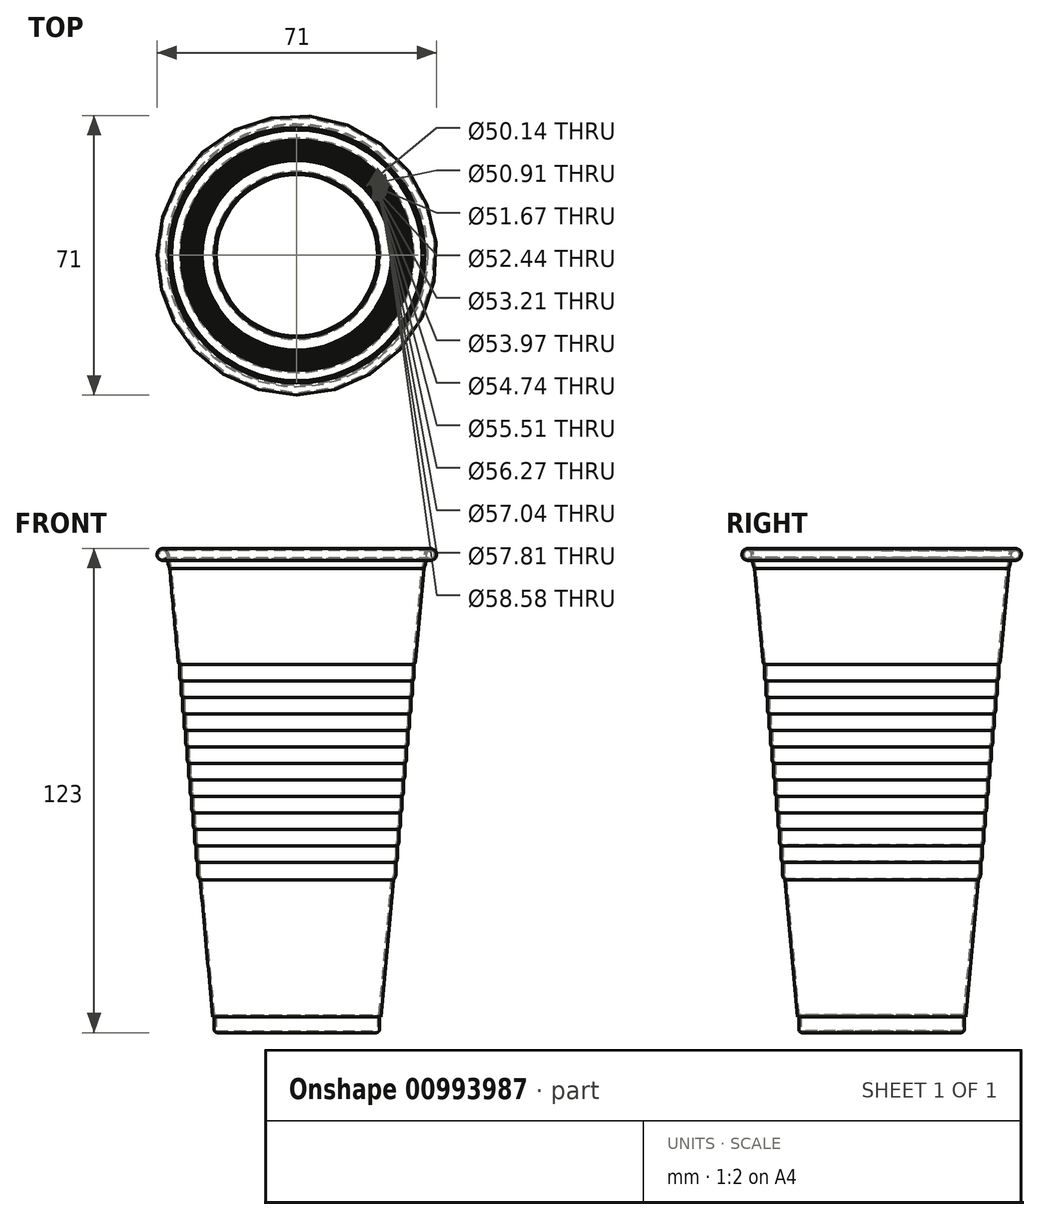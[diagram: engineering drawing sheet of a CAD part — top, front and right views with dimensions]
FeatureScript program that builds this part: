
annotation { "Feature Type Name" : "Feature", "Feature Type Description" : "" }
export const myFeature = defineFeature(function(context is Context, id is Id, definition is map)
    precondition{}
    {
        {
            var Q0;
            Q0=qCreatedBy(makeId("Front.planeOp"),FACE);
            var sketch = newSketch(context, id + "F0", { "sketchPlane" : qUnion([Q0])});
            skLineSegment(sketch, "E0", {"start": v(0, 0) * mm, "end": v(-21, 0) * mm});
            skLineSegment(sketch, "E1", {"start": v(-35.5, 123) * mm, "end": v(-32.27, 123) * mm});
            skLineSegment(sketch, "E2", {"start": v(-35.5, 123) * mm, "end": v(-35.5, 120) * mm});
            skLineSegment(sketch, "E3", {"start": v(-35.5, 120) * mm, "end": v(-32.5, 120) * mm});
            skLineSegment(sketch, "E4", {"start": v(-32.5, 120) * mm, "end": v(-25.18, 40.1) * mm});
            skPoint(sketch, "E5.centerSnap0", {"position": v(-35.5, 121.5) * mm});
            skLineSegment(sketch, "E6", {"start": v(-32.27, 123) * mm, "end": v(-29.67, 94.55) * mm});
            skLineSegment(sketch, "E7", {"start": v(0, 0) * mm, "end": v(0, 0.5) * mm});
            skLineSegment(sketch, "E8", {"start": v(0, 0.5) * mm, "end": v(-20.5, 0.5) * mm});
            skLineSegment(sketch, "E9", {"start": v(-21, 0) * mm, "end": v(-21, 4) * mm});
            skLineSegment(sketch, "E10", {"start": v(-21, 4) * mm, "end": v(-21.37, 4) * mm});
            skLineSegment(sketch, "E11", {"start": v(-20.91, 4.5) * mm, "end": v(-20.5, 4.5) * mm});
            skLineSegment(sketch, "E12", {"start": v(-20.5, 4.5) * mm, "end": v(-20.5, 0.5) * mm});
            skPoint(sketch, "E13.orphan", {"position": v(0, 123) * mm});
            skLineSegment(sketch, "E14", {"start": v(0, 0) * mm, "end": v(0, 123) * mm, "construction": true});
            skCircle(sketch, "E15", {"center": v(-34, 121.5) * mm, "radius": 1.5 * mm});
            skArc(sketch, "E16", {"start": v(-32.5, 121.5) * mm, "mid": v(-32.33, 119.72) * mm, "end": v(-31.81, 118) * mm});
            skCircle(sketch, "E17", {"center": v(-34, 121.5) * mm, "radius": 1 * mm});
            skArc(sketch, "E18", {"start": v(-33, 121.5) * mm, "mid": v(-32.82, 119.66) * mm, "end": v(-32.3, 117.88) * mm});
            skLineSegment(sketch, "E19", {"start": v(-34, 121.5) * mm, "end": v(-32.94, 120.44) * mm});
            skLineSegment(sketch, "E20", {"start": v(-32.5, 121.5) * mm, "end": v(-32.5, 120) * mm});
            skLineSegment(sketch, "E21", {"start": v(-34, 121.5) * mm, "end": v(-33, 121.5) * mm});
            skArc(sketch, "E22", {"start": v(-30.16, 94.5) * mm, "mid": v(-30.04, 93.97) * mm, "end": v(-29.79, 93.5) * mm});
            skPoint(sketch, "E23", {"position": v(-30.16, 94.5) * mm});
            skArc(sketch, "E24", {"start": v(-29.79, 90.5) * mm, "mid": v(-29.69, 89.88) * mm, "end": v(-29.4, 89.32) * mm});
            skLineSegment(sketch, "E25", {"start": v(-29.79, 93.5) * mm, "end": v(-29.79, 90.5) * mm});
            skArc(sketch, "E26", {"start": v(-29.4, 86.32) * mm, "mid": v(-29.3, 85.7) * mm, "end": v(-29.02, 85.13) * mm});
            skLineSegment(sketch, "E27", {"start": v(-29.4, 89.32) * mm, "end": v(-29.4, 86.32) * mm});
            skArc(sketch, "E28", {"start": v(-29.02, 82.13) * mm, "mid": v(-28.92, 81.5) * mm, "end": v(-28.64, 80.95) * mm});
            skLineSegment(sketch, "E29", {"start": v(-29.02, 85.13) * mm, "end": v(-29.02, 82.13) * mm});
            skLineSegment(sketch, "E30", {"start": v(-28.64, 80.95) * mm, "end": v(-28.64, 77.95) * mm});
            skArc(sketch, "E31.trimOffspring", {"start": v(-28.64, 77.95) * mm, "mid": v(-28.54, 77.32) * mm, "end": v(-28.25, 76.76) * mm});
            skArc(sketch, "E32", {"start": v(-28.25, 73.76) * mm, "mid": v(-28.16, 73.14) * mm, "end": v(-27.87, 72.58) * mm});
            skLineSegment(sketch, "E33", {"start": v(-28.25, 76.76) * mm, "end": v(-28.25, 73.76) * mm});
            skArc(sketch, "E34", {"start": v(-27.87, 69.58) * mm, "mid": v(-27.77, 68.96) * mm, "end": v(-27.49, 68.4) * mm});
            skArc(sketch, "E35", {"start": v(-27.49, 65.4) * mm, "mid": v(-27.39, 64.77) * mm, "end": v(-27.1, 64.2) * mm});
            skArc(sketch, "E36", {"start": v(-27.1, 61.2) * mm, "mid": v(-27, 60.59) * mm, "end": v(-26.72, 60.02) * mm});
            skLineSegment(sketch, "E37", {"start": v(-27.87, 72.58) * mm, "end": v(-27.87, 69.58) * mm});
            skLineSegment(sketch, "E38", {"start": v(-27.49, 68.4) * mm, "end": v(-27.49, 65.4) * mm});
            skLineSegment(sketch, "E39", {"start": v(-27.1, 64.2) * mm, "end": v(-27.1, 61.2) * mm});
            skLineSegment(sketch, "E40", {"start": v(-26.72, 60.02) * mm, "end": v(-26.72, 57.02) * mm});
            skArc(sketch, "E41", {"start": v(-26.72, 57.02) * mm, "mid": v(-26.62, 56.4) * mm, "end": v(-26.34, 55.84) * mm});
            skLineSegment(sketch, "E42", {"start": v(-26.34, 55.84) * mm, "end": v(-26.34, 52.84) * mm});
            skArc(sketch, "E43", {"start": v(-26.34, 52.84) * mm, "mid": v(-26.24, 52.22) * mm, "end": v(-25.95, 51.66) * mm});
            skLineSegment(sketch, "E44", {"start": v(-25.95, 51.66) * mm, "end": v(-25.95, 48.66) * mm});
            skArc(sketch, "E45", {"start": v(-25.95, 48.66) * mm, "mid": v(-25.85, 48.03) * mm, "end": v(-25.57, 47.47) * mm});
            skLineSegment(sketch, "E46", {"start": v(-25.57, 47.47) * mm, "end": v(-25.57, 44.47) * mm});
            skArc(sketch, "E47", {"start": v(-25.57, 44.47) * mm, "mid": v(-25.47, 43.85) * mm, "end": v(-25.19, 43.29) * mm});
            skLineSegment(sketch, "E48", {"start": v(-25.19, 43.29) * mm, "end": v(-25.19, 40.29) * mm});
            skArc(sketch, "E49", {"start": v(-25.19, 40.29) * mm, "mid": v(-25.02, 39.5) * mm, "end": v(-24.56, 38.82) * mm});
            skLineSegment(sketch, "E50", {"start": v(-21.37, 4) * mm, "end": v(-21, 0) * mm, "construction": true});
            skLineSegment(sketch, "E51", {"start": v(-20.91, 4.5) * mm, "end": v(-24.08, 39.07) * mm});
            skLineSegment(sketch, "E52", {"start": v(0, 0.5) * mm, "end": v(0, 0) * mm});
            skArc(sketch, "E53", {"start": v(-29.67, 94.55) * mm, "mid": v(-29.55, 94.08) * mm, "end": v(-29.29, 93.67) * mm});
            skArc(sketch, "E54", {"start": v(-29.29, 90.5) * mm, "mid": v(-29.19, 89.96) * mm, "end": v(-28.9, 89.5) * mm});
            skArc(sketch, "E55", {"start": v(-28.9, 86.32) * mm, "mid": v(-28.8, 85.78) * mm, "end": v(-28.52, 85.3) * mm});
            skArc(sketch, "E56", {"start": v(-26.99, 65.4) * mm, "mid": v(-26.89, 64.85) * mm, "end": v(-26.6, 64.38) * mm});
            skArc(sketch, "E57", {"start": v(-26.6, 61.2) * mm, "mid": v(-26.5, 60.67) * mm, "end": v(-26.22, 60.2) * mm});
            skLineSegment(sketch, "E58", {"start": v(-24.69, 43.46) * mm, "end": v(-24.69, 40.29) * mm});
            skArc(sketch, "E59.trimOffspring", {"start": v(-24.69, 40.29) * mm, "mid": v(-24.53, 39.6) * mm, "end": v(-24.08, 39.07) * mm});
            skLineSegment(sketch, "E60.trimOffspring", {"start": v(-24.56, 38.82) * mm, "end": v(-21.37, 4) * mm});
            skLineSegment(sketch, "E61", {"start": v(-25.07, 47.65) * mm, "end": v(-25.07, 44.47) * mm});
            skArc(sketch, "E62.trimOffspring", {"start": v(-25.07, 44.47) * mm, "mid": v(-24.97, 43.93) * mm, "end": v(-24.69, 43.46) * mm});
            skLineSegment(sketch, "E63", {"start": v(-29.29, 93.67) * mm, "end": v(-29.29, 90.5) * mm});
            skLineSegment(sketch, "E64", {"start": v(-28.9, 89.5) * mm, "end": v(-28.9, 86.32) * mm});
            skLineSegment(sketch, "E65", {"start": v(-28.52, 85.3) * mm, "end": v(-28.52, 82.13) * mm});
            skLineSegment(sketch, "E66", {"start": v(-28.14, 81.12) * mm, "end": v(-28.14, 77.95) * mm});
            skLineSegment(sketch, "E67", {"start": v(-27.75, 76.94) * mm, "end": v(-27.75, 73.76) * mm});
            skArc(sketch, "E68.trimOffspring", {"start": v(-28.14, 77.95) * mm, "mid": v(-28.04, 77.4) * mm, "end": v(-27.75, 76.94) * mm});
            skArc(sketch, "E69.trimOffspring", {"start": v(-27.75, 73.76) * mm, "mid": v(-27.65, 73.22) * mm, "end": v(-27.37, 72.75) * mm});
            skLineSegment(sketch, "E70", {"start": v(-25.45, 51.83) * mm, "end": v(-25.45, 48.66) * mm});
            skLineSegment(sketch, "E71", {"start": v(-25.84, 56.01) * mm, "end": v(-25.84, 52.84) * mm});
            skLineSegment(sketch, "E72", {"start": v(-26.22, 60.2) * mm, "end": v(-26.22, 57.02) * mm});
            skLineSegment(sketch, "E73", {"start": v(-26.6, 64.38) * mm, "end": v(-26.6, 61.2) * mm});
            skLineSegment(sketch, "E74", {"start": v(-26.99, 68.57) * mm, "end": v(-26.99, 65.4) * mm});
            skLineSegment(sketch, "E75", {"start": v(-27.37, 72.75) * mm, "end": v(-27.37, 69.58) * mm});
            skArc(sketch, "E76.trimOffspring", {"start": v(-27.37, 69.58) * mm, "mid": v(-27.27, 69.04) * mm, "end": v(-26.99, 68.57) * mm});
            skArc(sketch, "E77.trimOffspring", {"start": v(-28.52, 82.13) * mm, "mid": v(-28.42, 81.6) * mm, "end": v(-28.14, 81.12) * mm});
            skArc(sketch, "E78.trimOffspring", {"start": v(-25.45, 48.66) * mm, "mid": v(-25.35, 48.12) * mm, "end": v(-25.07, 47.65) * mm});
            skArc(sketch, "E79.trimOffspring", {"start": v(-25.84, 52.84) * mm, "mid": v(-25.74, 52.3) * mm, "end": v(-25.45, 51.83) * mm});
            skArc(sketch, "E80.trimOffspring", {"start": v(-26.22, 57.02) * mm, "mid": v(-26.12, 56.48) * mm, "end": v(-25.84, 56.01) * mm});
            skSolve(sketch);
        }
        {
            var Q0;
            Q0=qCreatedBy(makeId("Front.planeOp"),FACE);
            var sketch = newSketch(context, id + "F1", { "sketchPlane" : qUnion([Q0])});
            skArc(sketch, "E81.0.1", {"start": v(-33.36, 120.73) * mm, "mid": v(-34.9, 121.92) * mm, "end": v(-33, 121.5) * mm});
            skArc(sketch, "E81.0.4", {"start": v(-32.5, 121.5) * mm, "mid": v(-32.94, 122.56) * mm, "end": v(-34, 123) * mm});
            skArc(sketch, "E81.0.5", {"start": v(-34, 123) * mm, "mid": v(-35.06, 122.56) * mm, "end": v(-35.5, 121.5) * mm});
            skArc(sketch, "E81.0.6", {"start": v(-35.5, 121.5) * mm, "mid": v(-35.06, 120.44) * mm, "end": v(-34, 120) * mm});
            skArc(sketch, "E81.0.7", {"start": v(-34, 120) * mm, "mid": v(-33.49, 120.1) * mm, "end": v(-33.04, 120.35) * mm});
            skArc(sketch, "E82.0", {"start": v(-33, 121.5) * mm, "mid": v(-32.82, 119.66) * mm, "end": v(-32.3, 117.88) * mm});
            skArc(sketch, "E83.0", {"start": v(-32.5, 121.5) * mm, "mid": v(-32.33, 119.72) * mm, "end": v(-31.81, 118) * mm});
            skLineSegment(sketch, "E84.0", {"start": v(-31.81, 118) * mm, "end": v(-29.67, 94.55) * mm});
            skLineSegment(sketch, "E85.0", {"start": v(-32.3, 117.88) * mm, "end": v(-30.16, 94.5) * mm});
            skPoint(sketch, "E86.orphan", {"position": v(-32.27, 123) * mm});
            skPoint(sketch, "E87.orphan", {"position": v(-32.5, 120) * mm});
            skArc(sketch, "E88.0", {"start": v(-30.16, 94.5) * mm, "mid": v(-30.04, 93.97) * mm, "end": v(-29.79, 93.5) * mm});
            skLineSegment(sketch, "E89.0", {"start": v(-29.79, 93.5) * mm, "end": v(-29.79, 90.5) * mm});
            skArc(sketch, "E90.0", {"start": v(-29.79, 90.5) * mm, "mid": v(-29.69, 89.88) * mm, "end": v(-29.4, 89.32) * mm});
            skLineSegment(sketch, "E91.0", {"start": v(-29.4, 89.32) * mm, "end": v(-29.4, 86.32) * mm});
            skArc(sketch, "E92.0", {"start": v(-29.4, 86.32) * mm, "mid": v(-29.3, 85.7) * mm, "end": v(-29.02, 85.13) * mm});
            skLineSegment(sketch, "E93.0", {"start": v(-29.02, 85.13) * mm, "end": v(-29.02, 82.13) * mm});
            skArc(sketch, "E94.0", {"start": v(-29.02, 82.13) * mm, "mid": v(-28.92, 81.5) * mm, "end": v(-28.64, 80.95) * mm});
            skLineSegment(sketch, "E95.0", {"start": v(-28.64, 80.95) * mm, "end": v(-28.64, 77.95) * mm});
            skArc(sketch, "E96.0", {"start": v(-28.64, 77.95) * mm, "mid": v(-28.37, 76.95) * mm, "end": v(-27.64, 76.2) * mm});
            skLineSegment(sketch, "E97", {"start": v(-33.36, 120.73) * mm, "end": v(-33.04, 120.35) * mm});
            skPoint(sketch, "E81.0.0.end.orphan", {"position": v(-33.3, 120.8) * mm});
            skLineSegment(sketch, "E98", {"start": v(-34, 121.5) * mm, "end": v(-32.5, 121.5) * mm, "construction": true});
            skLineSegment(sketch, "E99.0", {"start": v(0, 0) * mm, "end": v(-21, 0) * mm});
            skLineSegment(sketch, "E100.0", {"start": v(0, 0.5) * mm, "end": v(-20.5, 0.5) * mm});
            skPoint(sketch, "E101.0", {"position": v(0, 0.25) * mm});
            skLineSegment(sketch, "E102.0", {"start": v(0, 0.5) * mm, "end": v(0, 0) * mm});
            skLineSegment(sketch, "E103.0", {"start": v(-21, 0) * mm, "end": v(-21, 4) * mm});
            skLineSegment(sketch, "E104.0", {"start": v(-20.5, 4.5) * mm, "end": v(-20.5, 0.5) * mm});
            skPoint(sketch, "E105.0", {"position": v(-21.18, 4) * mm});
            skLineSegment(sketch, "E106.0", {"start": v(-24.56, 38.82) * mm, "end": v(-21.37, 4) * mm});
            skLineSegment(sketch, "E107.0", {"start": v(-20.91, 4.5) * mm, "end": v(-24.08, 39.07) * mm});
            skPoint(sketch, "E108.0", {"position": v(-20.7, 4.5) * mm});
            skLineSegment(sketch, "E109.0", {"start": v(-20.91, 4.5) * mm, "end": v(-20.5, 4.5) * mm});
            skLineSegment(sketch, "E110.0", {"start": v(-21, 4) * mm, "end": v(-21.37, 4) * mm});
            skArc(sketch, "E111.0", {"start": v(-25.19, 40.29) * mm, "mid": v(-25.02, 39.5) * mm, "end": v(-24.56, 38.82) * mm});
            skArc(sketch, "E112.0", {"start": v(-24.69, 40.29) * mm, "mid": v(-24.53, 39.6) * mm, "end": v(-24.08, 39.07) * mm});
            skLineSegment(sketch, "E113.0", {"start": v(-24.69, 43.46) * mm, "end": v(-24.69, 40.29) * mm});
            skLineSegment(sketch, "E114.0", {"start": v(-25.19, 43.29) * mm, "end": v(-25.19, 40.29) * mm});
            skArc(sketch, "E115.0", {"start": v(-25.07, 44.47) * mm, "mid": v(-24.97, 43.93) * mm, "end": v(-24.69, 43.46) * mm});
            skLineSegment(sketch, "E116.0", {"start": v(-25.07, 47.65) * mm, "end": v(-25.07, 44.47) * mm});
            skArc(sketch, "E117.0", {"start": v(-25.45, 48.66) * mm, "mid": v(-25.35, 48.12) * mm, "end": v(-25.07, 47.65) * mm});
            skArc(sketch, "E118.0", {"start": v(-25.95, 48.66) * mm, "mid": v(-25.85, 48.03) * mm, "end": v(-25.57, 47.47) * mm});
            skLineSegment(sketch, "E119.0", {"start": v(-25.57, 47.47) * mm, "end": v(-25.57, 44.47) * mm});
            skArc(sketch, "E120.0", {"start": v(-25.57, 44.47) * mm, "mid": v(-25.47, 43.85) * mm, "end": v(-25.19, 43.29) * mm});
            skLineSegment(sketch, "E121.0", {"start": v(-25.45, 51.83) * mm, "end": v(-25.45, 48.66) * mm});
            skLineSegment(sketch, "E122.0", {"start": v(-25.95, 51.66) * mm, "end": v(-25.95, 48.66) * mm});
            skArc(sketch, "E123.0", {"start": v(-26.34, 52.84) * mm, "mid": v(-26.24, 52.22) * mm, "end": v(-25.95, 51.66) * mm});
            skArc(sketch, "E124.0", {"start": v(-25.84, 52.84) * mm, "mid": v(-25.74, 52.3) * mm, "end": v(-25.45, 51.83) * mm});
            skLineSegment(sketch, "E125.0", {"start": v(-25.84, 56.01) * mm, "end": v(-25.84, 52.84) * mm});
            skPoint(sketch, "E126.0", {"position": v(-26.34, 54.34) * mm});
            skLineSegment(sketch, "E127.0", {"start": v(-26.34, 55.84) * mm, "end": v(-26.34, 52.84) * mm});
            skArc(sketch, "E128.0", {"start": v(-26.72, 57.02) * mm, "mid": v(-26.62, 56.4) * mm, "end": v(-26.34, 55.84) * mm});
            skArc(sketch, "E129.0", {"start": v(-26.22, 57.02) * mm, "mid": v(-26.12, 56.48) * mm, "end": v(-25.84, 56.01) * mm});
            skLineSegment(sketch, "E130.0", {"start": v(-26.22, 60.2) * mm, "end": v(-26.22, 57.02) * mm});
            skLineSegment(sketch, "E131.0", {"start": v(-26.72, 60.02) * mm, "end": v(-26.72, 57.02) * mm});
            skLineSegment(sketch, "E132.0", {"start": v(-26.6, 64.38) * mm, "end": v(-26.6, 61.2) * mm});
            skLineSegment(sketch, "E133.0", {"start": v(-27.1, 64.2) * mm, "end": v(-27.1, 61.2) * mm});
            skArc(sketch, "E134.0", {"start": v(-27.1, 61.2) * mm, "mid": v(-27, 60.59) * mm, "end": v(-26.72, 60.02) * mm});
            skArc(sketch, "E135.0", {"start": v(-26.6, 61.2) * mm, "mid": v(-26.5, 60.67) * mm, "end": v(-26.22, 60.2) * mm});
            skArc(sketch, "E136.0", {"start": v(-27.49, 65.4) * mm, "mid": v(-27.39, 64.77) * mm, "end": v(-27.1, 64.2) * mm});
            skArc(sketch, "E137.0", {"start": v(-26.99, 65.4) * mm, "mid": v(-26.89, 64.85) * mm, "end": v(-26.6, 64.38) * mm});
            skLineSegment(sketch, "E138.0", {"start": v(-27.49, 68.4) * mm, "end": v(-27.49, 65.4) * mm});
            skLineSegment(sketch, "E139.0", {"start": v(-26.99, 68.57) * mm, "end": v(-26.99, 65.4) * mm});
            skArc(sketch, "E140.0", {"start": v(-27.37, 69.58) * mm, "mid": v(-27.27, 69.04) * mm, "end": v(-26.99, 68.57) * mm});
            skArc(sketch, "E141.0", {"start": v(-27.87, 69.58) * mm, "mid": v(-27.77, 68.96) * mm, "end": v(-27.49, 68.4) * mm});
            skLineSegment(sketch, "E142.0", {"start": v(-27.37, 72.75) * mm, "end": v(-27.37, 69.58) * mm});
            skLineSegment(sketch, "E143.0", {"start": v(-27.87, 72.58) * mm, "end": v(-27.87, 69.58) * mm});
            skArc(sketch, "E144.0", {"start": v(-28.25, 73.76) * mm, "mid": v(-28.16, 73.14) * mm, "end": v(-27.87, 72.58) * mm});
            skArc(sketch, "E145.0", {"start": v(-27.75, 73.76) * mm, "mid": v(-27.65, 73.22) * mm, "end": v(-27.37, 72.75) * mm});
            skLineSegment(sketch, "E146.0", {"start": v(-27.75, 76.94) * mm, "end": v(-27.75, 73.76) * mm});
            skLineSegment(sketch, "E147.0", {"start": v(-28.25, 76.76) * mm, "end": v(-28.25, 73.76) * mm});
            skArc(sketch, "E148.0", {"start": v(-28.64, 77.95) * mm, "mid": v(-28.54, 77.32) * mm, "end": v(-28.25, 76.76) * mm});
            skArc(sketch, "E149.0", {"start": v(-28.14, 77.95) * mm, "mid": v(-28.04, 77.4) * mm, "end": v(-27.75, 76.94) * mm});
            skLineSegment(sketch, "E150.0", {"start": v(-28.14, 81.12) * mm, "end": v(-28.14, 77.95) * mm});
            skPoint(sketch, "E151.0", {"position": v(-28.42, 81.6) * mm});
            skArc(sketch, "E152.0", {"start": v(-28.52, 82.13) * mm, "mid": v(-28.42, 81.6) * mm, "end": v(-28.14, 81.12) * mm});
            skLineSegment(sketch, "E153.0", {"start": v(-28.52, 85.3) * mm, "end": v(-28.52, 82.13) * mm});
            skPoint(sketch, "E154.0", {"position": v(-28.8, 85.78) * mm});
            skArc(sketch, "E155.0", {"start": v(-28.9, 86.32) * mm, "mid": v(-28.8, 85.78) * mm, "end": v(-28.52, 85.3) * mm});
            skLineSegment(sketch, "E156.0", {"start": v(-28.9, 89.5) * mm, "end": v(-28.9, 86.32) * mm});
            skArc(sketch, "E157.0", {"start": v(-29.29, 90.5) * mm, "mid": v(-29.19, 89.96) * mm, "end": v(-28.9, 89.5) * mm});
            skArc(sketch, "E158.0", {"start": v(-29.67, 94.55) * mm, "mid": v(-29.55, 94.08) * mm, "end": v(-29.29, 93.67) * mm});
            skLineSegment(sketch, "E159.0", {"start": v(-29.29, 93.67) * mm, "end": v(-29.29, 90.5) * mm});
            skSolve(sketch);
        }
        {
            var Q0;
            Q0 = qSketchRegion(id + "F1", true);
            var Q1;
            Q1=sQuery(id+"F0.wireOp",EDGE,"E14");
            revolve(context, id + "F2", {"surfaceOperationType" : NewSurfaceOperationType.NEW, "entities" : qUnion([Q0]), "axis" : qUnion([Q1]), "revolveType" : RevolveType.FULL});
        }
        {
            var Q0;
            Q0=makeQuery(id+"F2.opRevolve","SWEPT_EDGE",EDGE,{"disambiguationData":[OSD([sQuery(id+"F1.wireOp",EDGE,"E99.0"),sQuery(id+"F1.wireOp",EDGE,"E103.0")])]});
            fillet(context, id + "F3", {"entities" : qUnion([Q0]), "radius" : 0.8 * mm, "tangentPropagation" : true, "allowEdgeOverflow" : false});
        }
    });
